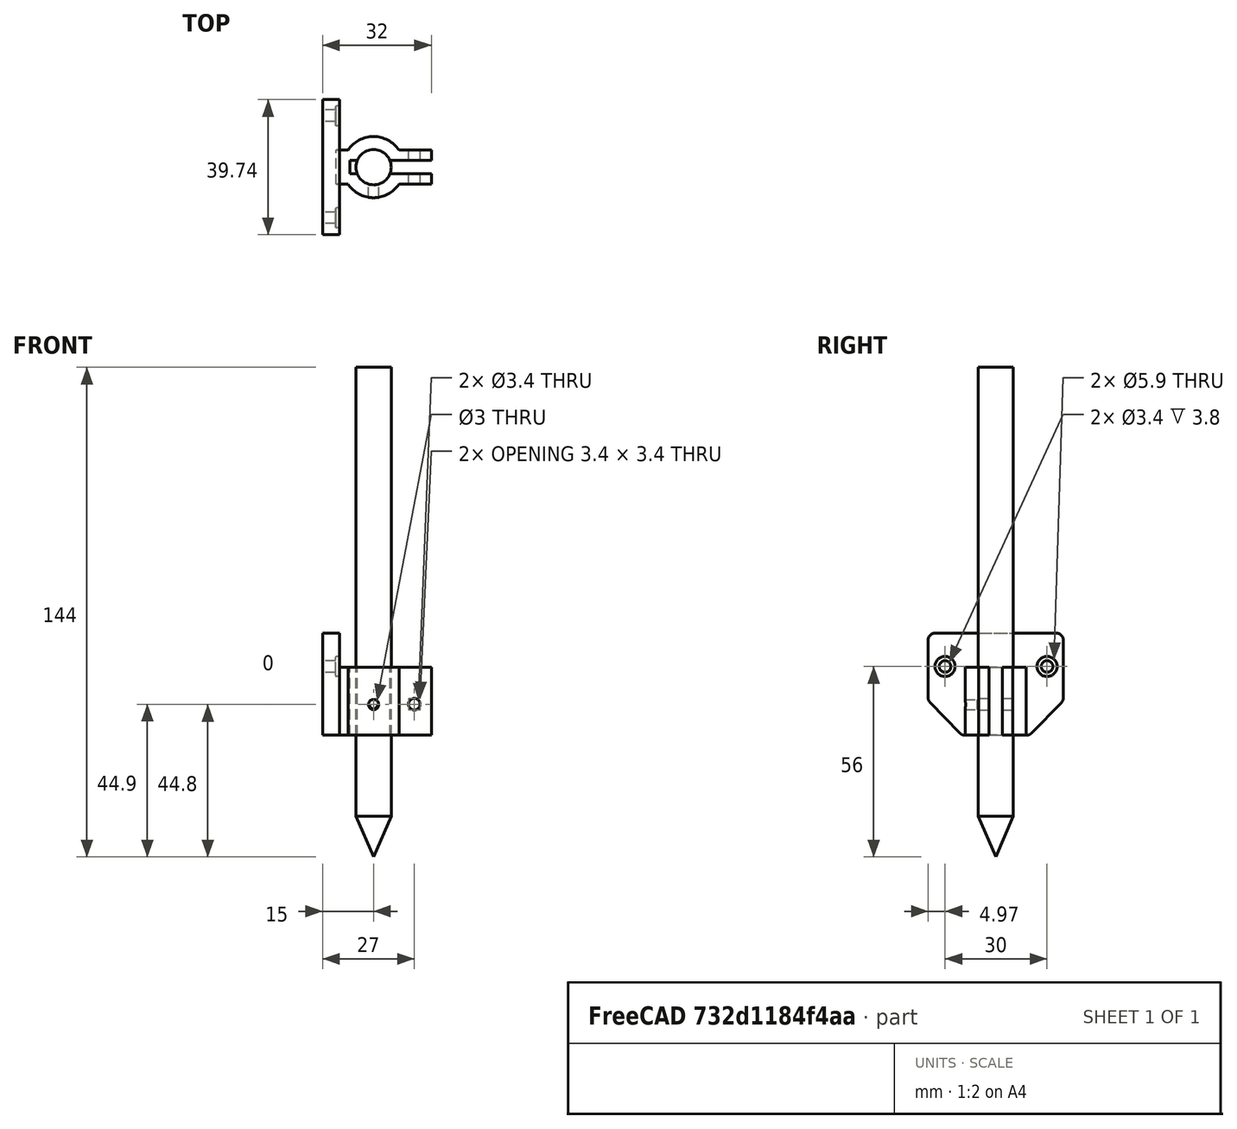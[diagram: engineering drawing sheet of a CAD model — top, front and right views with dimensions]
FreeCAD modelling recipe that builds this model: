
FCSTD DOCUMENT  (FreeCAD 0.14R3702 (Git))
Label: copia de cabezal_plotter
License: CC-BY 3.0
LicenseURL: http://creativecommons.org/licenses/by/3.0/
objects: Part::MultiFuse×7, Part::Cut×5, Part::Feature×4, Part::Offset×3, Part::Box×2, Part::Cylinder×2, Mesh::Feature×1, Sketcher::SketchObject×1, PartDesign::Pad×1, Part::Cone×1, Part::Fillet×1
note: 28 computed .brp shape members not serialized (recipe doc carries the construction recipe); baked Part::Feature solids carry a one-line shape summary decoded from their .brp

FEATURE [Mesh::Feature] __Carro_eje_X_x1  label="1-Carro eje X x1"
  Placement = pos=(-15,117,99.6) rot=(0.707107,0,-0.707107;3.14159rad)
FEATURE [Part::Feature] Part__Feature  label="Chamfer001"
  shape: bbox 5.5 x 5.5 x 23 mm, 16 faces (baked)
FEATURE [Part::Offset] Offset
  Fill = false
  Intersection = false
  Join = 0
  Mode = 0
  Placement = pos=(0,-14.9,4) rot=(0,0,1;0rad)
  SelfIntersection = false
  Source = -> Part__Feature
  Value = 0.2
FEATURE [Part::Feature] Part__Feature001  label="Chamfer002"
  shape: bbox 5.5 x 5.5 x 23 mm, 16 faces (baked)
FEATURE [Part::Offset] Offset001
  Fill = false
  Intersection = false
  Join = 0
  Mode = 0
  Placement = pos=(0,15.1,4) rot=(0,0,1;0rad)
  SelfIntersection = false
  Source = -> Part__Feature001
  Value = 0.2
FEATURE [Sketcher::SketchObject] Sketch
  sketch-geometry (6):
    g0: LineSegment StartX=-9.79451 StartY=19.8719 StartZ=0 EndX=10.0386 EndY=19.8719 EndZ=0
    g1: LineSegment StartX=10.0386 StartY=19.8719 StartZ=0 EndX=20.1958 EndY=9.99067 EndZ=0
    g2: LineSegment StartX=20.1958 StartY=9.99067 StartZ=0 EndX=20.1958 EndY=-9.99067 EndZ=0
    g3: LineSegment StartX=20.1958 StartY=-9.99067 StartZ=0 EndX=10.0386 EndY=-19.8719 EndZ=0
    g4: LineSegment StartX=10.0386 StartY=-19.8719 StartZ=0 EndX=-9.79451 EndY=-19.8719 EndZ=0
    g5: LineSegment StartX=-9.79451 StartY=-19.8719 StartZ=0 EndX=-9.79451 EndY=19.8719 EndZ=0
  constraints (13):
    c: Horizontal(g0)
    c: Coincident(g0,g1)
    c: Coincident(g1,g2)
    c: Vertical(g2)
    c: Coincident(g2,g3)
    c: Coincident(g3,g4)
    c: Horizontal(g4)
    c: Coincident(g4,g5)
    c: Coincident(g5,g0)
    c: Vertical(g5)
    c: Symmetric(g4,g0,g-1)
    c: Symmetric(g0,g3,g-1)
    c: Symmetric(g1,g2,g-1)
FEATURE [PartDesign::Pad] Pad
  Length = 5
  Length2 = 100
  Sketch = -> Sketch
  Type = 0
FEATURE [Part::MultiFuse] Fusion
  Shapes = -> [Offset001,Offset]
FEATURE [Part::Cut] Cut
  Base = -> Pad
  Tool = -> Fusion
FEATURE [Part::Box] Box  label="Cubo"
  Height = 20
  Length = 28
  Placement = pos=(-11,-5,0) rot=(0,0,1;0rad)
  Width = 10
FEATURE [Part::Cylinder] Cylinder  label="Cilindro"
  Angle = 360
  Height = 132
  Radius = 5.2
FEATURE [Part::Cone] Cone  label="Cono"
  Angle = 360
  Height = 12
  Placement = pos=(0,0,-12) rot=(0,0,1;0rad)
  Radius1 = 0
  Radius2 = 5.2
FEATURE [Part::MultiFuse] Fusion001  label="Boligrafo"
  Placement = pos=(0,0,-24) rot=(0,0,1;0rad)
  Shapes = -> [Cylinder,Cone]
FEATURE [Part::Cylinder] Cylinder001  label="Cilindro001"
  Angle = 360
  Height = 20
  Radius = 9
FEATURE [Part::Feature] Part__Feature002  label="Chamfer003"
  shape: bbox 5.5 x 5.5 x 23 mm, 16 faces (baked)
FEATURE [Part::Offset] Offset002
  Fill = false
  Intersection = false
  Join = 0
  Mode = 0
  Placement = pos=(12,-8,9.1) rot=(1,0,0;1.5708rad)
  SelfIntersection = false
  Source = -> Part__Feature002
  Value = 0.2
FEATURE [Part::Box] Box001  label="Cubo001"
  Height = 22
  Length = 27
  Placement = pos=(-7,-2,-1) rot=(0,0,1;0rad)
  Width = 4
FEATURE [Part::Feature] Part__Feature003  label="Chamfer004"
  Placement = pos=(0,-25,9) rot=(1,0,0;1.5708rad)
  shape: bbox 5.5 x 23 x 5.5 mm, 16 faces (baked)
FEATURE [Part::MultiFuse] Fusion002
  Shapes = -> [Box,Cylinder001]
FEATURE [Part::Cut] Cut001
  Base = -> Fusion002
  Tool = -> Fusion001
FEATURE [Part::Cut] Cut002
  Base = -> Cut001
  Tool = -> Box001
FEATURE [Part::MultiFuse] Fusion004  label="Boligrafo001"
  Placement = pos=(0,0,-24) rot=(0,0,1;0rad)
  Shapes = -> [Cylinder,Cone]
FEATURE [Part::MultiFuse] Fusion005
  Placement = pos=(0,0,3) rot=(0,0,1;0rad)
  Shapes = -> [Offset001,Offset]
FEATURE [Part::Cut] Cut004  label="Base"
  Base = -> Cut
  Placement = pos=(-15,0,20) rot=(0,1,0;1.5708rad)
  Tool = -> Fusion005
FEATURE [Part::MultiFuse] Fusion003
  Shapes = -> [Offset002,Part__Feature003]
FEATURE [Part::Cut] Cut003  label="SujetaBoli"
  Base = -> Cut002
  Placement = pos=(0,0,-0.2) rot=(0,0,1;0rad)
  Tool = -> Fusion003
FEATURE [Part::MultiFuse] Fusion006  label="Plotter"
  Shapes = -> [Cut003,Cut004]
FEATURE [Part::Fillet] Fillet  label="Plotter_redondeado"
  Base = -> Fusion006
  Edges = 6 edges r=2: [Edge35,Edge37,Edge70,Edge72,Edge74,Edge76]
